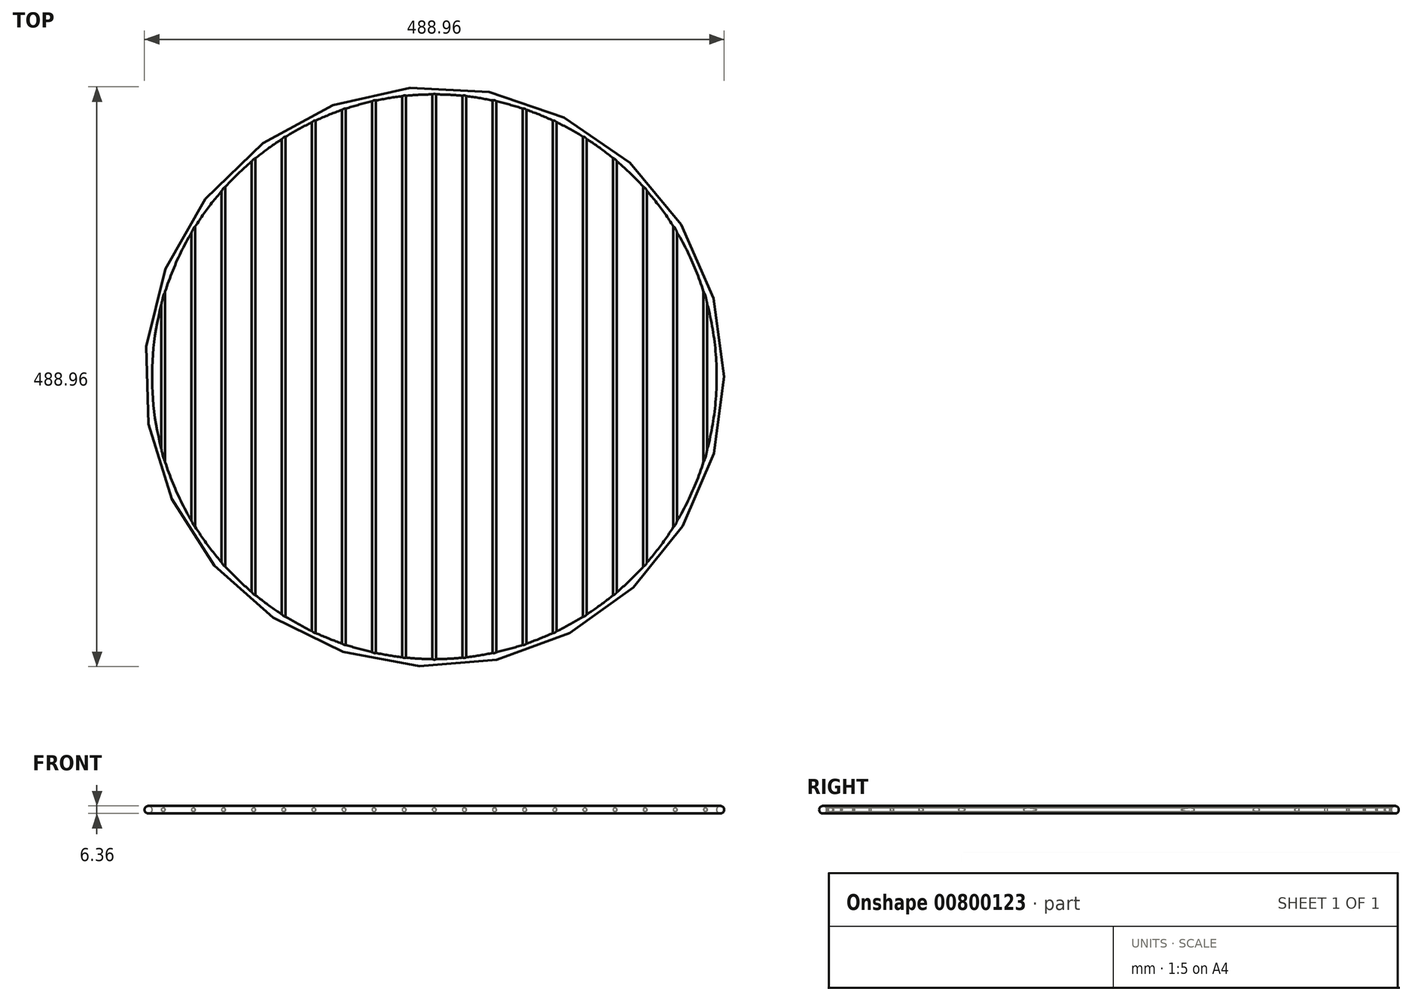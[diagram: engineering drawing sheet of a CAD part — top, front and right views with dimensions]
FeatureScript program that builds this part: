
annotation { "Feature Type Name" : "Feature", "Feature Type Description" : "" }
export const myFeature = defineFeature(function(context is Context, id is Id, definition is map)
    precondition{}
    {
        {
            var Q0;
            Q0=qCreatedBy(makeId("Front.planeOp"),FACE);
            var sketch = newSketch(context, id + "F0", { "sketchPlane" : qUnion([Q0])});
            skCircle(sketch, "E0", {"center": v(241.3, 0) * mm, "radius": 3.18 * mm});
            skLineSegment(sketch, "E1", {"start": v(0, 0) * mm, "end": v(0, 32.12) * mm, "construction": true});
            skSolve(sketch);
        }
        {
            var Q0;
            Q0=qCreatedBy(makeId("Front.planeOp"),FACE);
            var sketch = newSketch(context, id + "F1", { "sketchPlane" : qUnion([Q0])});
            skCircle(sketch, "E2", {"center": v(0, 0) * mm, "radius": 1.59 * mm});
            skCircle(sketch, "E3.1.0.0", {"center": v(25.4, 0) * mm, "radius": 1.59 * mm});
            skCircle(sketch, "E3.2.0.0", {"center": v(50.8, 0) * mm, "radius": 1.59 * mm});
            skCircle(sketch, "E3.3.0.0", {"center": v(76.2, 0) * mm, "radius": 1.59 * mm});
            skCircle(sketch, "E3.4.0.0", {"center": v(101.6, 0) * mm, "radius": 1.59 * mm});
            skCircle(sketch, "E3.5.0.0", {"center": v(127, 0) * mm, "radius": 1.59 * mm});
            skCircle(sketch, "E3.6.0.0", {"center": v(152.4, 0) * mm, "radius": 1.59 * mm});
            skCircle(sketch, "E3.7.0.0", {"center": v(177.8, 0) * mm, "radius": 1.59 * mm});
            skCircle(sketch, "E3.8.0.0", {"center": v(203.2, 0) * mm, "radius": 1.59 * mm});
            skCircle(sketch, "E3.9.0.0", {"center": v(228.6, 0) * mm, "radius": 1.59 * mm});
            skLineSegment(sketch, "E3.direction1", {"start": v(0, 0) * mm, "end": v(25.4, 0) * mm, "construction": true});
            skCircle(sketch, "E4.1.0.0", {"center": v(-25.4, 0) * mm, "radius": 1.59 * mm});
            skCircle(sketch, "E4.2.0.0", {"center": v(-50.8, 0) * mm, "radius": 1.59 * mm});
            skCircle(sketch, "E4.3.0.0", {"center": v(-76.2, 0) * mm, "radius": 1.59 * mm});
            skCircle(sketch, "E4.4.0.0", {"center": v(-101.6, 0) * mm, "radius": 1.59 * mm});
            skCircle(sketch, "E4.5.0.0", {"center": v(-127, 0) * mm, "radius": 1.59 * mm});
            skCircle(sketch, "E4.6.0.0", {"center": v(-152.4, 0) * mm, "radius": 1.59 * mm});
            skCircle(sketch, "E4.7.0.0", {"center": v(-177.8, 0) * mm, "radius": 1.59 * mm});
            skCircle(sketch, "E4.8.0.0", {"center": v(-203.2, 0) * mm, "radius": 1.59 * mm});
            skCircle(sketch, "E4.9.0.0", {"center": v(-228.6, 0) * mm, "radius": 1.59 * mm});
            skLineSegment(sketch, "E4.direction1", {"start": v(0, 0) * mm, "end": v(-25.4, 0) * mm, "construction": true});
            skSolve(sketch);
        }
        {
            var Q0;
            Q0=makeQuery(id+"F0.imprint","IMPRINT",FACE,{"disambiguationData":[TD([[makeQuery(id+"F0.imprint","IMPRINT",EDGE,{"derivedFrom":sQuery(id+"F0.wireOp",EDGE,"E0")}),1.0]])]});
            var Q1;
            Q1=sQuery(id+"F0.wireOp",EDGE,"E1");
            revolve(context, id + "F2", {"surfaceOperationType" : NewSurfaceOperationType.NEW, "entities" : qUnion([Q0]), "axis" : qUnion([Q1]), "revolveType" : RevolveType.FULL});
        }
        {
            var Q0;
            Q0 = qSketchRegion(id + "F1", true);
            extrude(context, id + "F3", {"entities" : qUnion([Q0]), "operationType" : NewBodyOperationType.ADD, "endBound" : BoundingType.UP_TO_NEXT, "depth" : 25.4 * mm, "offsetDistance" : 25.4 * mm, "hasSecondDirection" : true, "secondDirectionBound" : BoundingType.UP_TO_NEXT, "secondDirectionOppositeDirection" : true, "secondDirectionDepth" : 25.4 * mm});
        }
    });
